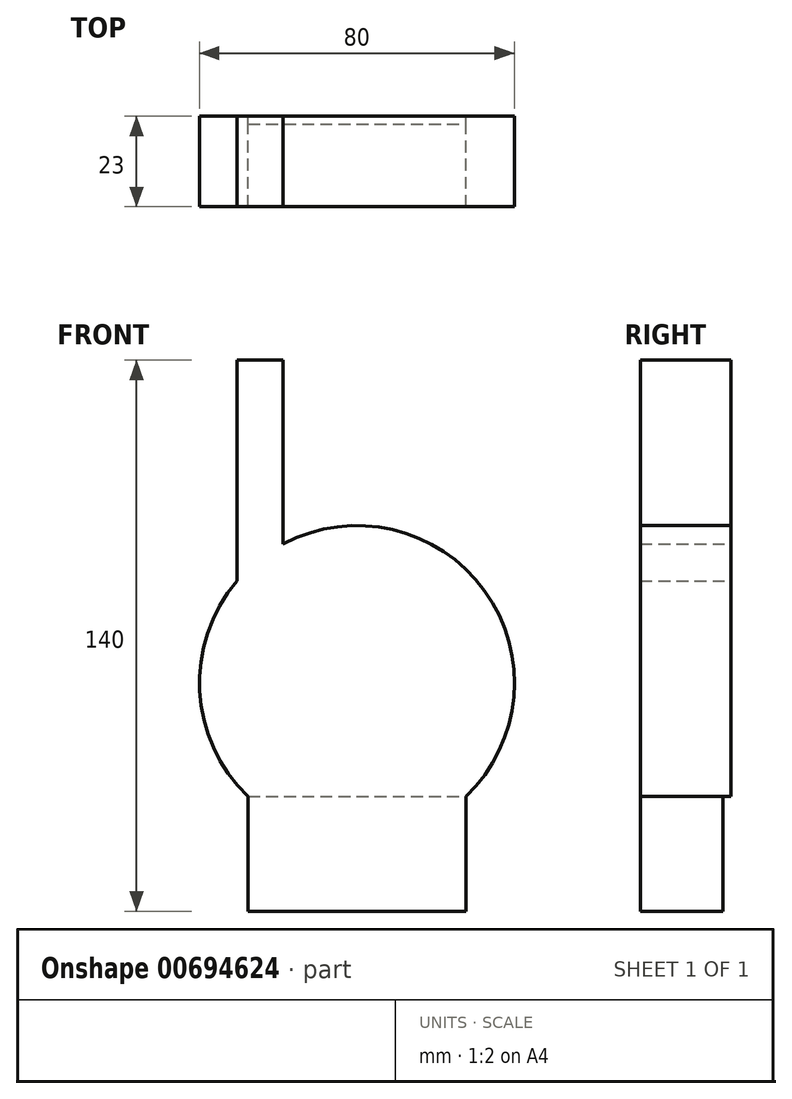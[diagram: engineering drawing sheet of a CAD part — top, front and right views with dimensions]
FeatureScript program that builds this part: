
annotation { "Feature Type Name" : "Feature", "Feature Type Description" : "" }
export const myFeature = defineFeature(function(context is Context, id is Id, definition is map)
    precondition{}
    {
        {
            var Q0;
            Q0=qCreatedBy(makeId("Front.planeOp"),FACE);
            var sketch = newSketch(context, id + "F0", { "sketchPlane" : qUnion([Q0])});
            skArc(sketch, "E0", {"start": v(58.7, -83.5) * mm, "mid": v(63.42, -31.2) * mm, "end": v(12.27, -19.3) * mm});
            skLineSegment(sketch, "E1", {"start": v(3.32, -83.5) * mm, "end": v(3.32, -112.64) * mm});
            skLineSegment(sketch, "E2", {"start": v(3.32, -112.64) * mm, "end": v(58.7, -112.64) * mm});
            skLineSegment(sketch, "E3", {"start": v(58.7, -112.64) * mm, "end": v(58.7, -83.5) * mm});
            skLineSegment(sketch, "E4", {"start": v(0.55, -28.7) * mm, "end": v(0.55, 27.36) * mm});
            skLineSegment(sketch, "E5", {"start": v(0.55, 27.36) * mm, "end": v(12.27, 27.36) * mm});
            skLineSegment(sketch, "E6", {"start": v(12.27, 27.36) * mm, "end": v(12.27, -19.3) * mm});
            skArc(sketch, "E7.trimOffspring", {"start": v(0.55, -28.7) * mm, "mid": v(-8.94, -56.66) * mm, "end": v(3.32, -83.5) * mm});
            skSolve(sketch);
        }
        {
            var Q0;
            Q0=qSketchRegion(id+"F0",true);
            extrude(context, id + "F1", {"entities" : qUnion([Q0]), "depth" : 23 * mm, "offsetDistance" : 25 * mm});
        }
        {
            var Q0;
            Q0=makeQuery(id+"F1.opExtrude","CAP_FACE",FACE,{"disambiguationData":[OSD([sQuery(id+"F0.wireOp",EDGE,"E0"),sQuery(id+"F0.wireOp",EDGE,"E1"),sQuery(id+"F0.wireOp",EDGE,"E2"),sQuery(id+"F0.wireOp",EDGE,"E3"),sQuery(id+"F0.wireOp",EDGE,"E4"),sQuery(id+"F0.wireOp",EDGE,"E5"),sQuery(id+"F0.wireOp",EDGE,"E6"),sQuery(id+"F0.wireOp",EDGE,"E7.trimOffspring")])],"isStart":true});
            var sketch = newSketch(context, id + "F2", { "sketchPlane" : qUnion([Q0])});
            skLineSegment(sketch, "E8.bottom", {"start": v(-3.32, -112.64) * mm, "end": v(-58.7, -112.64) * mm});
            skLineSegment(sketch, "E8.top", {"start": v(-3.32, -83.5) * mm, "end": v(-58.7, -83.5) * mm});
            skLineSegment(sketch, "E8.left", {"start": v(-3.32, -112.64) * mm, "end": v(-3.32, -83.5) * mm});
            skLineSegment(sketch, "E8.right", {"start": v(-58.7, -112.64) * mm, "end": v(-58.7, -83.5) * mm});
            skSolve(sketch);
        }
        {
            var Q0;
            Q0=qSketchRegion(id+"F2",true);
            extrude(context, id + "F3", {"entities" : qUnion([Q0]), "operationType" : NewBodyOperationType.REMOVE, "oppositeDirection" : true, "depth" : 2 * mm, "offsetDistance" : 25 * mm});
        }
    });
